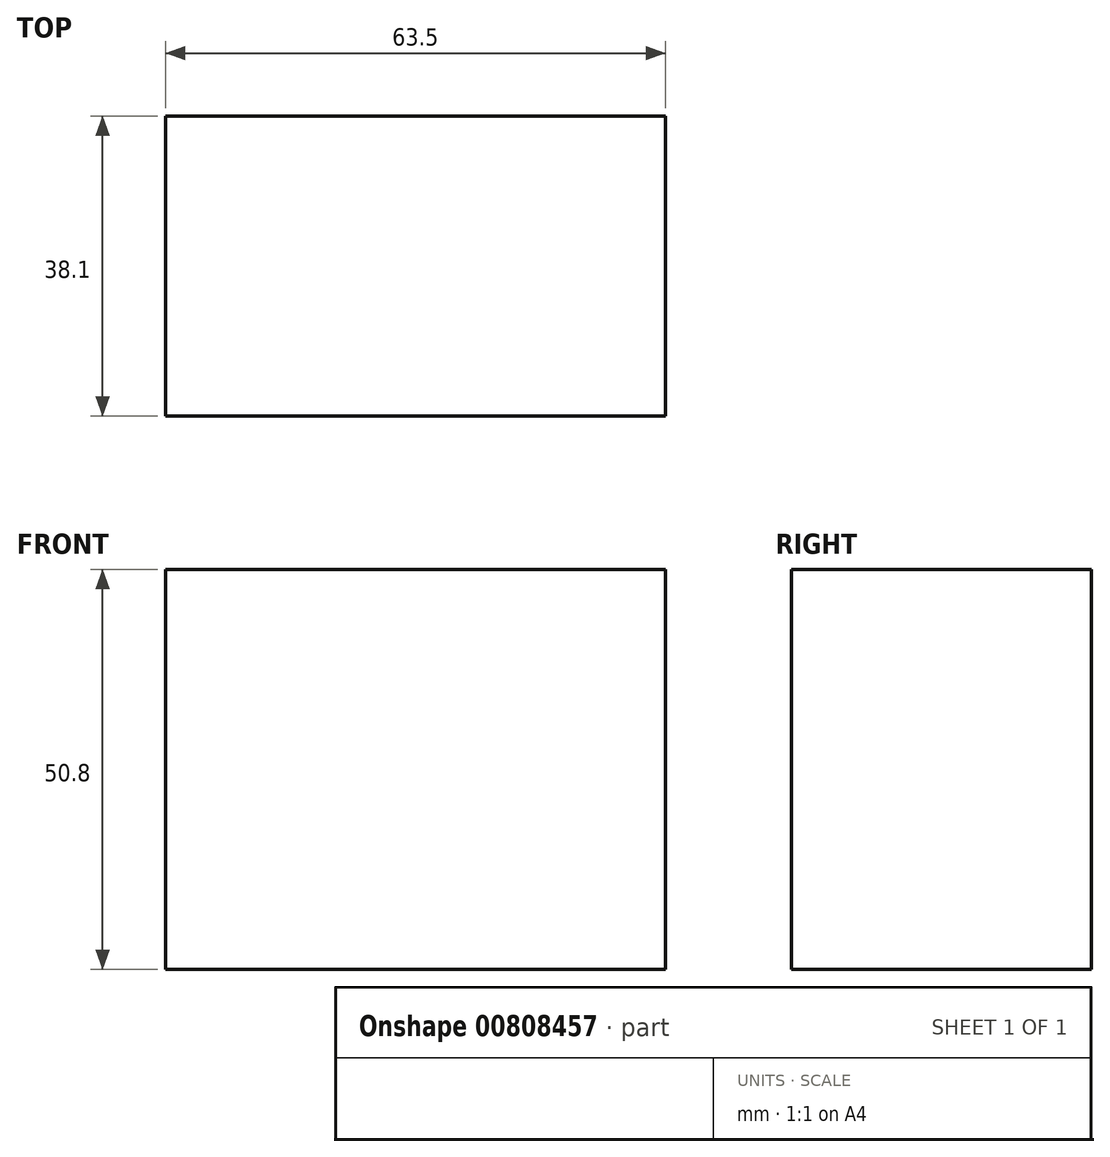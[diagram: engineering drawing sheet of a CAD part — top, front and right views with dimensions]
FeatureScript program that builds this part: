
annotation { "Feature Type Name" : "Feature", "Feature Type Description" : "" }
export const myFeature = defineFeature(function(context is Context, id is Id, definition is map)
    precondition{}
    {
        {
            var Q0;
            Q0=qCreatedBy(makeId("Front.planeOp"),FACE);
            var sketch = newSketch(context, id + "F0", { "sketchPlane" : qUnion([Q0])});
            skLineSegment(sketch, "E0", {"start": v(0, 0) * mm, "end": v(0, 50.8) * mm});
            skLineSegment(sketch, "E1", {"start": v(0, 50.8) * mm, "end": v(63.5, 50.8) * mm});
            skLineSegment(sketch, "E2", {"start": v(63.5, 50.8) * mm, "end": v(63.5, 0) * mm});
            skLineSegment(sketch, "E3", {"start": v(63.5, 0) * mm, "end": v(0, 0) * mm});
            skSolve(sketch);
        }
        {
            var Q0;
            Q0=makeQuery(id+"F0.imprint","IMPRINT",FACE,{"disambiguationData":[TD([[makeQuery(id+"F0.imprint","IMPRINT",EDGE,{"derivedFrom":sQuery(id+"F0.wireOp",EDGE,"E0")}),-1.0]])]});
            extrude(context, id + "F1", {"entities" : qUnion([Q0]), "depth" : 38.1 * mm, "offsetDistance" : 25.4 * mm});
        }
    });
